# Revit family: M_Valve_Balancing and Control_MEPcontent_Oventrop_Hydromat DTR 10647
name_source: partatom
category: Pipe Accessories
revit_build: Autodesk Revit 2015 (Build: 20140223_1515(x64)
units: mm (PartAtom-declared; Revit-internal decimal feet)

## types (6) — shared parameters
Angle = 50.00°
Article Description = Differential pressure regulator
Article Type = Hydromat DTR 10647
BonnetPlastic = Color RGB 35-35-35
Bronze = Color RGB 156-122-90
Content Supplier URL = www.mepcontent.eu
Custom = No
D_Bonnet = 104 mm
Description = Differential pressure regulator
EMCS Version = 2.0
ETIM Article Class = EC011463
Family Version = 10.14
Hb4 = 18 mm  [stored 0.0590551 ft]
Hb5 = 3 mm  [stored 0.00984252 ft]
Hlp1 = 22 mm  [stored 0.0721785 ft]
IFCExportAs = IfcValveType
IFCExportType = PRESSUREREDUCING
Lgt2 = 11 mm  [stored 0.0360892 ft]
MEPcontent Class = VALVE_BALANCING
Manufacturer = Oventrop
Manufacturer URL = http://www.oventrop.de
Model = Hydromat DTR 10647
Pressure Drop = 0.0 Pa
Product Line = Oventrop
R1_Bonnet = 23.026 mm
R2_Bonnet = 31.2 mm
Rcut_Bonnet = 22.026 mm
Revit Version = 2015
URL = www.stabiplan.com
r1 = 2 mm  [stored 0.00656168 ft]
r2 = 3 mm  [stored 0.00984252 ft]
r3_Bonnet = 14.857 mm

## per-type parameters (varying)
| type | Dist_elem | Female_Port_Width | GTIN | H1_Bonnet | H_Bonnet | Hb1 | Hb2 | Hb3 | Hb6 | Height | L2 | Length | Lgt1 | Manufacturer Art. No. | NominalDiameter | Nut_Dimension | OuterDiameter | Rad1 | Rad2 | Rad3 | Rad4 | Rad5 | SW2 |
| DN 40 | 45 mm | 19.1 mm  [stored 0.062664 ft] | 4026755324631 | 43.076 mm | 178 mm | 212.224 mm | 50 mm | 5 mm  [stored 0.0164042 ft] | 67.186 mm | 178 mm | 11.261 mm | 120 mm | 21.1 mm  [stored 0.0692257 ft] | 1064712 | 38.100 mm | 54 mm | 48.3 mm | 24.15 mm | 24.15 mm | 26.65 mm | 29.15 mm | 31.15 mm | 62.354 mm |
| DN 32 | 45 mm | 19.1 mm  [stored 0.062664 ft] | 4026755324624 | 41.624 mm | 172 mm | 204.392 mm | 50 mm | 1 mm  [stored 0.00328084 ft] | 63.806 mm | 172 mm | 9.886 mm | 110 mm | 21.1 mm  [stored 0.0692257 ft] | 1064710 | 31.750 mm | 50 mm | 42.4 mm | 21.2 mm  [stored 0.0695538 ft] | 21.2 mm  [stored 0.0695538 ft] | 23.7 mm | 26.2 mm | 28.2 mm | 57.735 mm |
| DN 25 | 39 mm | 16.8 mm  [stored 0.0551181 ft] | 4026755324617 | 39.446 mm | 163 mm | 192.643 mm | 50 mm | 13 mm | 81.313 mm | 163 mm | 7.857 mm | 97.5 mm | 18.8 mm  [stored 0.0616798 ft] | 1064708 | 25.400 mm | 41 mm | 33.7 mm | 16.85 mm  [stored 0.0552822 ft] | 16.85 mm  [stored 0.0552822 ft] | 19.35 mm  [stored 0.0634843 ft] | 21.85 mm | 23.85 mm | 47.343 mm |
| DN 20 | 40 mm | 14.5 mm  [stored 0.0475722 ft] | 4026755324600 | 38.72 mm | 160 mm | 188.727 mm | 21.43 mm  [stored 0.0703084 ft] | 11 mm  [stored 0.0360892 ft] | 43.248 mm | 160 mm | 6.272 mm | 84 mm | 16.5 mm  [stored 0.0541339 ft] | 1064706 | 19.050 mm | 32 mm | 26.9 mm | 13.45 mm | 13.45 mm | 15.95 mm | 18.45 mm | 20.45 mm | 36.95 mm |
| DN 15 | 37 mm | 13.2 mm  [stored 0.0433071 ft] | 4026755324594 | 38.236 mm | 158 mm | 186.116 mm | 17.62 mm  [stored 0.0578084 ft] | 15 mm  [stored 0.0492126 ft] | 45.337 mm | 158 mm | 4.966 mm | 80 mm | 15.2 mm | 1064704 | 12.700 mm | 27 mm | 21.3 mm  [stored 0.0698819 ft] | 10.65 mm  [stored 0.0349409 ft] | 10.65 mm  [stored 0.0349409 ft] | 13.15 mm  [stored 0.043143 ft] | 15.65 mm | 17.65 mm | 31.177 mm |
| DN 50 | 67 mm | 25.7 mm | 4026755305586 | 50.82 mm | 210 mm | 253.997 mm | 50 mm | 5 mm  [stored 0.0164042 ft] | 63.503 mm | 210 mm | 14.059 mm | 150 mm | 27.7 mm | 1064716 | 50.800 mm | 70 mm | 60.3 mm | 30.15 mm | 30.15 mm | 32.65 mm | 35.15 mm | 37.15 mm | 80.829 mm |

note: [stored X ft] marks values corroborated as IEEE doubles in the binary element streams (Revit-internal decimal feet)

## geometry (parser evidence)
native form markers: Sweep x3
no freeform markers — native parametric forms only
